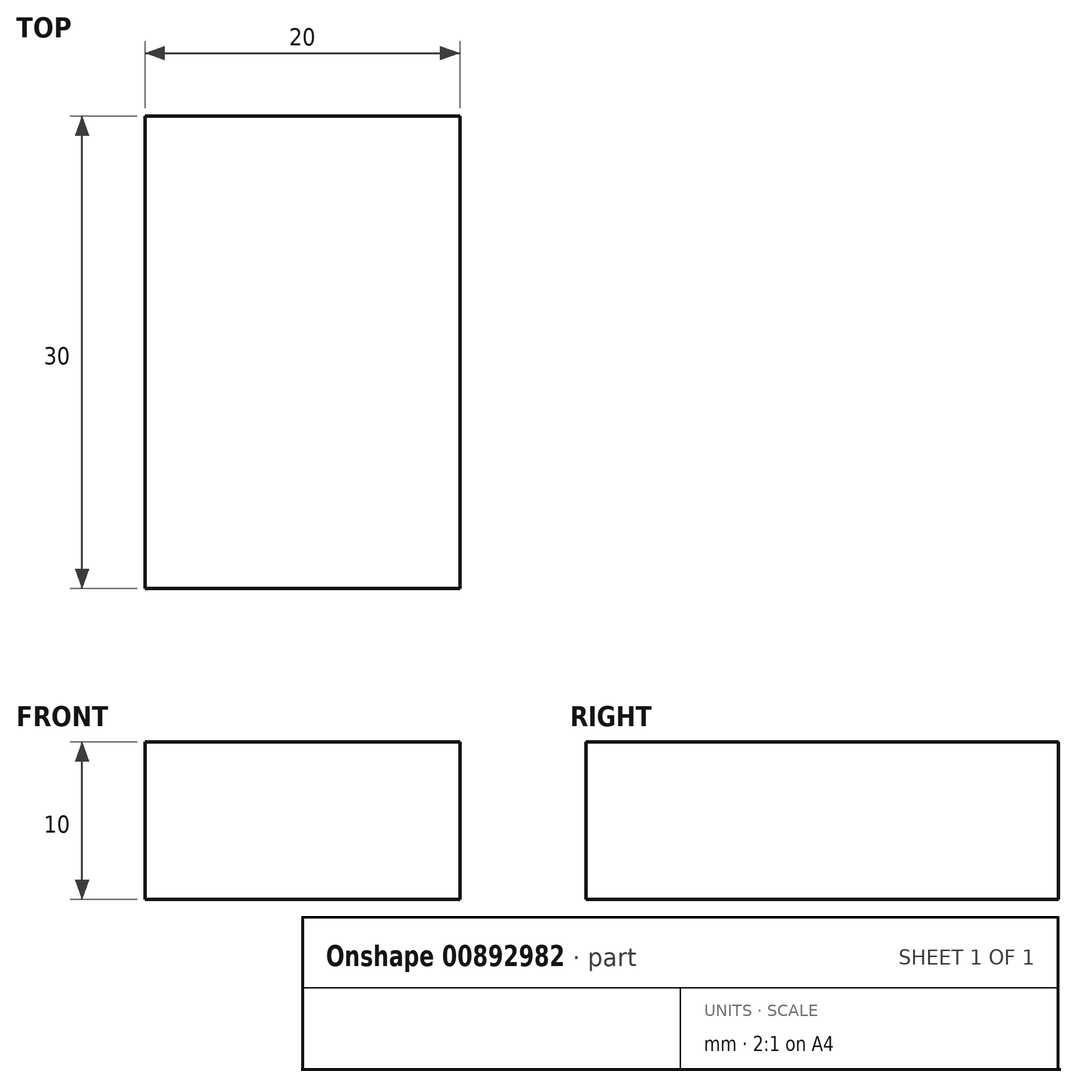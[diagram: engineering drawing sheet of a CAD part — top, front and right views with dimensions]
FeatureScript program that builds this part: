
annotation { "Feature Type Name" : "Feature", "Feature Type Description" : "" }
export const myFeature = defineFeature(function(context is Context, id is Id, definition is map)
    precondition{}
    {
        {
            var Q0;
            Q0=qCreatedBy(makeId("Top.planeOp"),FACE);
            var sketch = newSketch(context, id + "F0", { "sketchPlane" : qUnion([Q0])});
            skLineSegment(sketch, "E0.bottom", {"start": v(10, 15) * mm, "end": v(-10, 15) * mm});
            skLineSegment(sketch, "E0.top", {"start": v(10, -15) * mm, "end": v(-10, -15) * mm});
            skLineSegment(sketch, "E0.left", {"start": v(10, 15) * mm, "end": v(10, -15) * mm});
            skLineSegment(sketch, "E0.right", {"start": v(-10, 15) * mm, "end": v(-10, -15) * mm});
            skSolve(sketch);
        }
        {
            var Q0;
            Q0=makeQuery(id+"F0.imprint","IMPRINT",FACE,{"disambiguationData":[TD([[makeQuery(id+"F0.imprint","IMPRINT",EDGE,{"derivedFrom":sQuery(id+"F0.wireOp",EDGE,"E0.bottom")}),1.0]])]});
            extrude(context, id + "F1", {"entities" : qUnion([Q0]), "depth" : 10 * mm, "offsetDistance" : 25 * mm});
        }
    });
